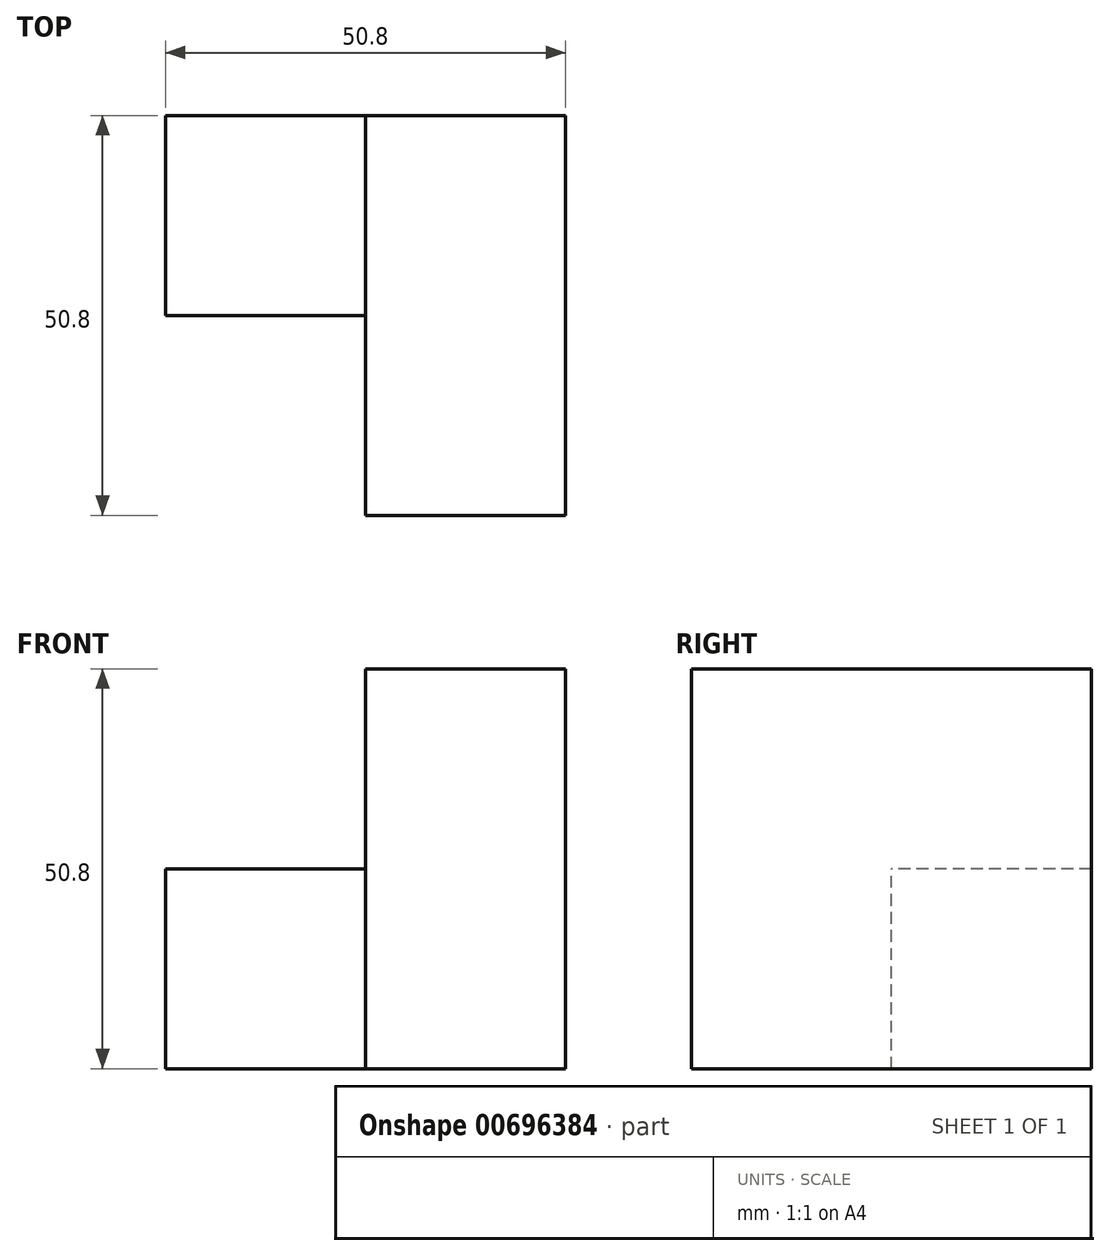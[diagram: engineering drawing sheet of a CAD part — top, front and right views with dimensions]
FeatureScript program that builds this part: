
annotation { "Feature Type Name" : "Feature", "Feature Type Description" : "" }
export const myFeature = defineFeature(function(context is Context, id is Id, definition is map)
    precondition{}
    {
        {
            var Q0;
            Q0=qCreatedBy(makeId("Front.planeOp"),FACE);
            var sketch = newSketch(context, id + "F0", { "sketchPlane" : qUnion([Q0])});
            skLineSegment(sketch, "E0.bottom", {"start": v(-21.86, 0) * mm, "end": v(-47.26, 0) * mm});
            skLineSegment(sketch, "E0.top", {"start": v(-21.86, 50.8) * mm, "end": v(-47.26, 50.8) * mm});
            skLineSegment(sketch, "E0.left", {"start": v(-21.86, 0) * mm, "end": v(-21.86, 50.8) * mm});
            skLineSegment(sketch, "E1", {"start": v(-47.26, 50.8) * mm, "end": v(-47.26, 0) * mm});
            skPoint(sketch, "E0.right.end.orphan", {"position": v(-72.66, 50.8) * mm});
            skPoint(sketch, "E2.orphan", {"position": v(-72.66, 0) * mm});
            skSolve(sketch);
        }
        {
            var Q0;
            Q0=makeQuery(id+"F0.imprint","IMPRINT",FACE,{"disambiguationData":[TD([[makeQuery(id+"F0.imprint","IMPRINT",EDGE,{"derivedFrom":sQuery(id+"F0.wireOp",EDGE,"E0.bottom")}),-1.0]])]});
            extrude(context, id + "F1", {"entities" : qUnion([Q0]), "depth" : 50.8 * mm, "offsetDistance" : 25.4 * mm});
        }
        {
            var Q0;
            Q0=makeQuery(id+"F1.opExtrude","SWEPT_FACE",FACE,{"disambiguationData":[OSD([sQuery(id+"F0.wireOp",EDGE,"E1")])]});
            var sketch = newSketch(context, id + "F2", { "sketchPlane" : qUnion([Q0])});
            skLineSegment(sketch, "E3.bottom", {"start": v(0, 0) * mm, "end": v(25.4, 0) * mm});
            skLineSegment(sketch, "E3.top", {"start": v(0, 25.4) * mm, "end": v(25.4, 25.4) * mm});
            skLineSegment(sketch, "E3.left", {"start": v(0, 0) * mm, "end": v(0, 25.4) * mm});
            skLineSegment(sketch, "E3.right", {"start": v(25.4, 0) * mm, "end": v(25.4, 25.4) * mm});
            skSolve(sketch);
        }
        {
            var Q0;
            Q0=makeQuery(id+"F2.imprint","IMPRINT",FACE,{"disambiguationData":[TD([[makeQuery(id+"F2.imprint","IMPRINT",EDGE,{"derivedFrom":sQuery(id+"F2.wireOp",EDGE,"E3.bottom")}),-1.0]])]});
            extrude(context, id + "F3", {"entities" : qUnion([Q0]), "operationType" : NewBodyOperationType.ADD, "depth" : 25.4 * mm, "offsetDistance" : 25.4 * mm});
        }
    });
